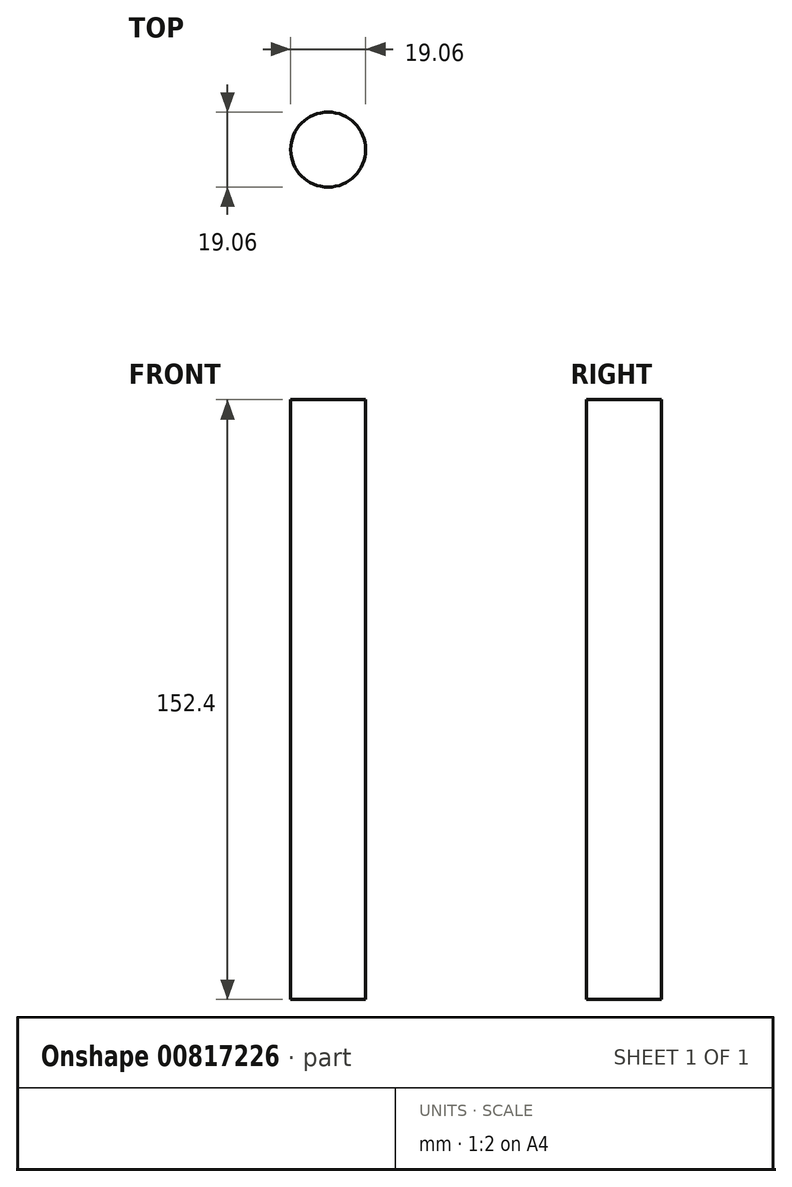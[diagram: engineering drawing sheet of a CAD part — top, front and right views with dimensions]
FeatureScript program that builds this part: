
annotation { "Feature Type Name" : "Feature", "Feature Type Description" : "" }
export const myFeature = defineFeature(function(context is Context, id is Id, definition is map)
    precondition{}
    {
        {
            var Q0;
            Q0=qCreatedBy(makeId("Top.planeOp"),FACE);
            var sketch = newSketch(context, id + "F0", { "sketchPlane" : qUnion([Q0])});
            skCircle(sketch, "E0", {"center": v(0, 0) * mm, "radius": 9.53 * mm});
            skSolve(sketch);
        }
        {
            var Q0;
            Q0=sQuery(id+"F0.wireOp",EDGE,"E0");
            extrude(context, id + "F1", {"bodyType" : ToolBodyType.SURFACE, "surfaceEntities" : qUnion([Q0]), "depth" : 152.4 * mm, "offsetDistance" : 25.4 * mm});
        }
    });
